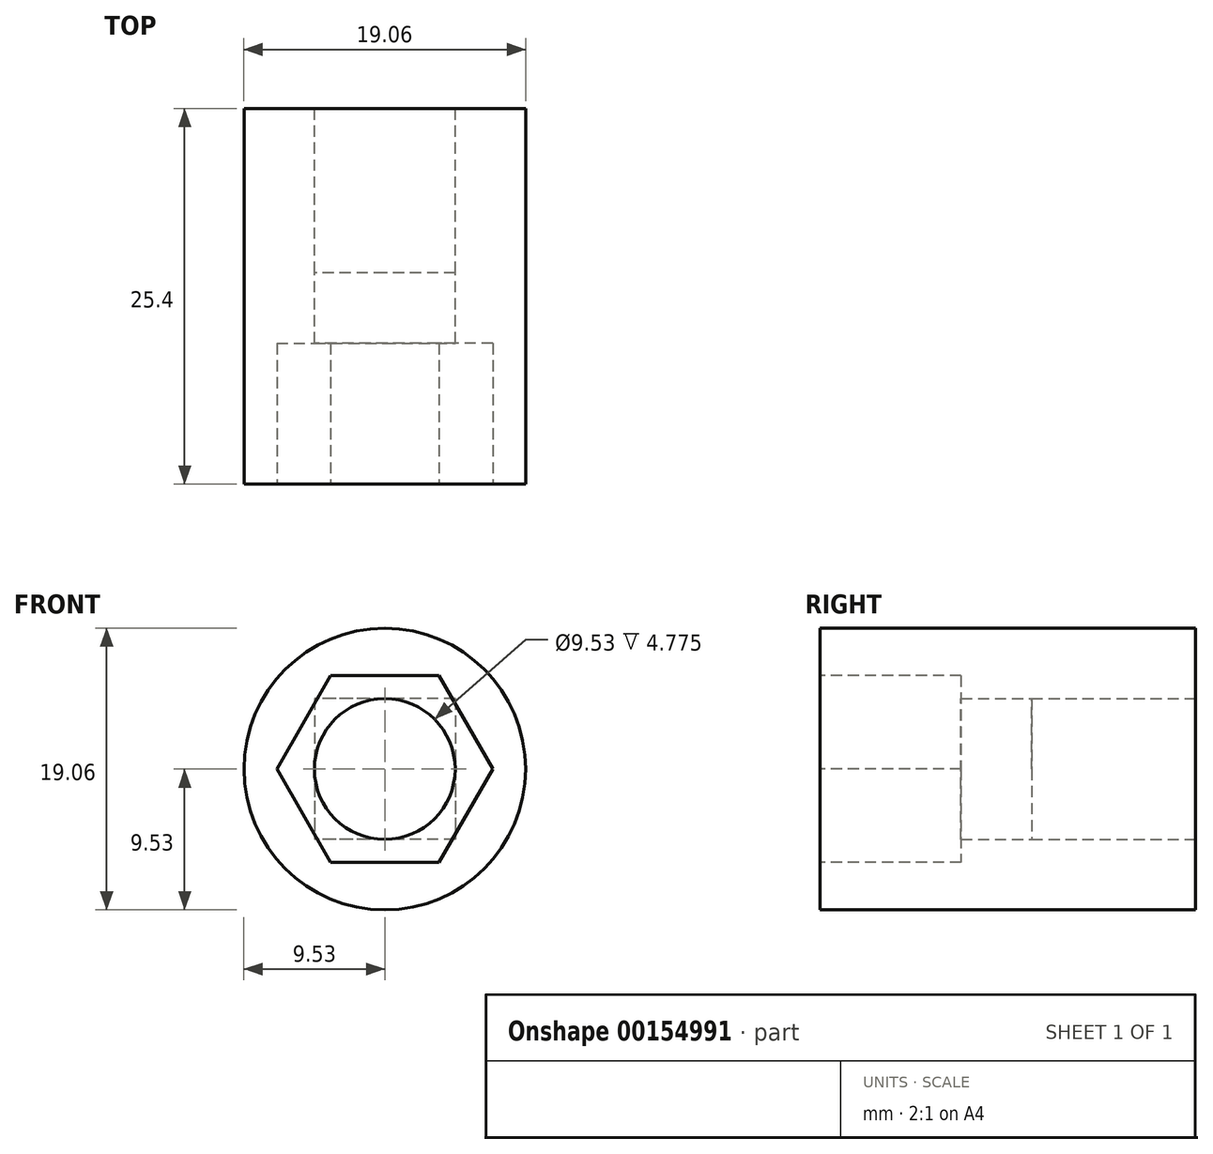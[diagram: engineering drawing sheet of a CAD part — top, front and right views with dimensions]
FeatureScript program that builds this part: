
annotation { "Feature Type Name" : "Feature", "Feature Type Description" : "" }
export const myFeature = defineFeature(function(context is Context, id is Id, definition is map)
    precondition{}
    {
        {
            var Q0;
            Q0=qCreatedBy(makeId("Front.planeOp"),FACE);
            var sketch = newSketch(context, id + "F0", { "sketchPlane" : qUnion([Q0])});
            skCircle(sketch, "E0", {"center": v(0, 0) * mm, "radius": 9.52 * mm});
            skSolve(sketch);
        }
        {
            var Q0;
            Q0 = qSketchRegion(id + "F0", true);
            extrude(context, id + "F1", {"entities" : qUnion([Q0]), "depth" : 25.4 * mm});
        }
        {
            var Q0;
            Q0=qCreatedBy(makeId("Front.planeOp"),FACE);
            var sketch = newSketch(context, id + "F2", { "sketchPlane" : qUnion([Q0])});
            skLineSegment(sketch, "E1.bottom", {"start": v(4.76, 4.76) * mm, "end": v(-4.76, 4.76) * mm});
            skLineSegment(sketch, "E1.top", {"start": v(4.76, -4.76) * mm, "end": v(-4.76, -4.76) * mm});
            skLineSegment(sketch, "E1.left", {"start": v(4.76, 4.76) * mm, "end": v(4.76, -4.76) * mm});
            skLineSegment(sketch, "E1.right", {"start": v(-4.76, 4.76) * mm, "end": v(-4.76, -4.76) * mm});
            skPoint(sketch, "E1.middle", {"position": v(0, 0) * mm});
            skCircle(sketch, "E2", {"center": v(0, 0) * mm, "radius": 4.76 * mm});
            skSolve(sketch);
        }
        {
            var Q0;
            {var subQ0=sQuery(id+"F2.wireOp",EDGE,"E2");var subQ1=makeQuery(id+"F2.imprint","INTERSECT",VERTEX,{"derivedFrom":[sQuery(id+"F2.wireOp",EDGE,"E1.bottom"),subQ0]});Q0=makeQuery(id+"F2.imprint","IMPRINT",FACE,{"disambiguationData":[TD([[makeQuery(id+"F2.imprint","IMPRINT",EDGE,{"disambiguationData":[TD([[subQ1,1.0]])],"derivedFrom":subQ0}),1.0]])]});}
            extrude(context, id + "F3", {"entities" : qUnion([Q0]), "operationType" : NewBodyOperationType.REMOVE, "endBound" : BoundingType.THROUGH_ALL, "depth" : 25.4 * mm});
        }
        {
            var Q0;
            Q0 = qSketchRegion(id + "F2", true);
            extrude(context, id + "F4", {"entities" : qUnion([Q0]), "operationType" : NewBodyOperationType.REMOVE, "depth" : 11.1 * mm});
        }
        {
            var Q0;
            Q0=makeQuery(id+"F1.opExtrude","CAP_FACE",FACE,{"disambiguationData":[OSD([sQuery(id+"F0.wireOp",EDGE,"E0")])],"isStart":false});
            var sketch = newSketch(context, id + "F5", { "sketchPlane" : qUnion([Q0])});
            skCircle(sketch, "E3.cCircle", {"center": v(0, 0) * mm, "radius": 6.32 * mm, "construction": true});
            skLineSegment(sketch, "E3.0", {"start": v(3.65, -6.32) * mm, "end": v(-3.65, -6.32) * mm});
            skLineSegment(sketch, "E3.1", {"start": v(-3.65, -6.32) * mm, "end": v(-7.3, 0) * mm});
            skLineSegment(sketch, "E3.2", {"start": v(-7.3, 0) * mm, "end": v(-3.65, 6.32) * mm});
            skLineSegment(sketch, "E3.3", {"start": v(-3.65, 6.32) * mm, "end": v(3.65, 6.32) * mm});
            skLineSegment(sketch, "E3.4", {"start": v(3.65, 6.32) * mm, "end": v(7.3, 0) * mm});
            skLineSegment(sketch, "E3.5", {"start": v(7.3, 0) * mm, "end": v(3.65, -6.32) * mm});
            skPoint(sketch, "E3.0.midPoint", {"position": v(0, -6.32) * mm});
            skSolve(sketch);
        }
        {
            var Q0;
            Q0 = qSketchRegion(id + "F5", true);
            extrude(context, id + "F6", {"entities" : qUnion([Q0]), "operationType" : NewBodyOperationType.REMOVE, "oppositeDirection" : true, "depth" : 9.52 * mm});
        }
    });
